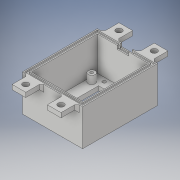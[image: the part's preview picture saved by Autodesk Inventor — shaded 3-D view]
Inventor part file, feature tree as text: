
AUTODESK INVENTOR PART (.ipt)
format: ipt  version: 2019 (Build 230136000, 136)  size: 608,256 bytes
history: native  units: mm
features: extrude x10, sketch x10, projected_geometry x9, chamfer x4, mirror x1
ambient origin geometry x8: Origin, YZ Plane, XZ Plane, XY Plane, X Axis, Y Axis, Z Axis, Center Point
bodies: Solid1 (feature_tree)
feature tree (34):
  extrude  "Extrusion1"  Depth=20.0mm
  extrude  "Extrusion3"  Depth=53.0mm
  extrude  "Extrusion4"  Depth=25.5mm
  extrude  "Extrusion5"  Depth=13.0mm
  chamfer  "Chamfer1"  Distance=4.0mm
  chamfer  "Chamfer3"  Distance=4.0mm
  extrude  "Extrusion9"  Depth=30.0mm TaperAngle=0.0deg
  chamfer  "Chamfer4"  Distance=40.0mm
  extrude  "Extrusion10"  Depth=25.0mm
  mirror  "Mirror2"
  extrude  "Extrusion11"  Depth=15.0mm TaperAngle=0.0deg
  extrude  "Extrusion12"  Depth=12.0mm
  extrude  "Extrusion13"  Depth=4.0mm
  chamfer  "Chamfer5"  Distance=5.0mm
  extrude  "Extrusion14"  Depth=7.0mm
  sketch  "Sketch2"  dims[d17=2.9mm d18=20.0mm d20=51.0mm d21=20.0mm d23=26.0mm]
  sketch  "Sketch4"  dims[d26=66.0mm d27=53.0mm]
  projected_geometry  "Projected Loop2"
  sketch  "Sketch5"  dims[d28=25.5mm d29=25.5mm]
  sketch  "Sketch6"  dims[d30=13.0mm d31=13.0mm]
  projected_geometry  "Projected Loop3"
  sketch  "Sketch10"  dims[d33=3.2mm]
  projected_geometry  "Projected Loop6"
  sketch  "Sketch11"  dims[d42=20.0mm]
  projected_geometry  "Projected Loop7"
  projected_geometry  "Projected Loop8"
  sketch  "Sketch14"  dims[d43=20.0mm d50=4.0mm d51=0.0mm]
  projected_geometry  "Projected Loop10"
  sketch  "Sketch15"  dims[d54=4.0mm]
  projected_geometry  "Projected Loop11"
  sketch  "Sketch16"  dims[d55=4.0mm]
  projected_geometry  "Projected Loop12"
  sketch  "Sketch17"  dims[d56=4.0mm d57=4.0mm d58=30.0mm d59=0.0mm d61=40.0mm d62=25.0mm d63=15.0mm d64=0.0mm d65=12.0mm d66=4.0mm d67=5.0mm d68=19.5mm d69=14.0mm d70=0.0mm d75=2.0mm d76=2.0mm d77=45.0deg d81=2.0mm d82=2.0mm d83=45.0deg d98=12.0mm d99=4.0mm d100=5.0mm d101=14.0mm d102=0.0mm d103=2.0mm d104=2.0mm d105=45.0deg d106=5.2mm d107=5.2mm d108=14.0mm d109=0.0mm d110=48.0mm d111=24.0mm d112=21.0mm d113=10.5mm d114=1.0mm d115=1.0mm d116=2.0mm d117=2.0mm d118=2.0mm d119=2.0mm d120=1.2mm d121=0.0mm d122=6.0mm d123=6.0mm d124=6.0mm d125=6.0mm d126=10.0mm d127=3.0mm d128=2.5mm d129=2.5mm d130=10.0mm d131=0.0mm d132=2.0mm d133=1.0mm d134=1.2mm d135=0.0mm d136=2.0mm d137=2.0mm d138=45.0deg d139=20.0mm d141=40.0mm d142=20.0mm d144=37.0mm d147=9.0mm d148=9.0mm d149=4.0mm d150=4.0mm d151=2.5mm d152=20.0mm d154=40.0mm d155=20.0mm d157=37.0mm d160=6.0mm d161=7.0mm d162=0.0mm d163=2.9mm d164=2.9mm d165=2.9mm]
  projected_geometry  "Projected Loop13"
